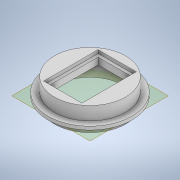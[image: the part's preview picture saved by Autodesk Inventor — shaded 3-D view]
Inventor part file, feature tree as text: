
AUTODESK INVENTOR PART (.ipt)
format: ipt  version: 2020 (Build 240168000, 168)  size: 147,968 bytes
history: native  units: in
note: dims shown in document units (in); Inventor stores cm internally (conversion verified against a paired STEP export)
features: extrude x5, sketch x5, plane x1
ambient origin geometry x8: Origin, YZ Plane, XZ Plane, XY Plane, X Axis, Y Axis, Z Axis, Center Point
bodies: Solid1 (feature_tree)
feature tree (11):
  extrude  "Extrusion1"  Depth=2.4in
  extrude  "Extrusion2"  Depth=0.375in TaperAngle=0.0deg
  extrude  "Extrusion3"  Depth=2.025in
  extrude  "Extrusion4"  Depth=1.2in
  plane  "Work Plane1"
  extrude  "Extrusion5"  TaperAngle=0.0deg  [1 undecoded]
  sketch  "Sketch1"  dims[d0=2.65in d1=2.4in]
  sketch  "Sketch2"  dims[d2=0.5in d3=0.0in d4=0.375in d5=0.0in]
  sketch  "Sketch3"  dims[d6=1.425in d7=2.025in]
  sketch  "Sketch4"  dims[d8=0.125in d9=0.0in d10=1.2in]
  sketch  "Sketch5"  dims[d11=1.8in d12=0.0in d13=0.0in d14=-0.25in d15=3.125in d16=0.125in d17=0.0in]
note: 1 required parameter value undecoded (feature->parameter linkage not recoverable at this tier; creation-order binding heuristic only, values carry confidence <= 0.55)
